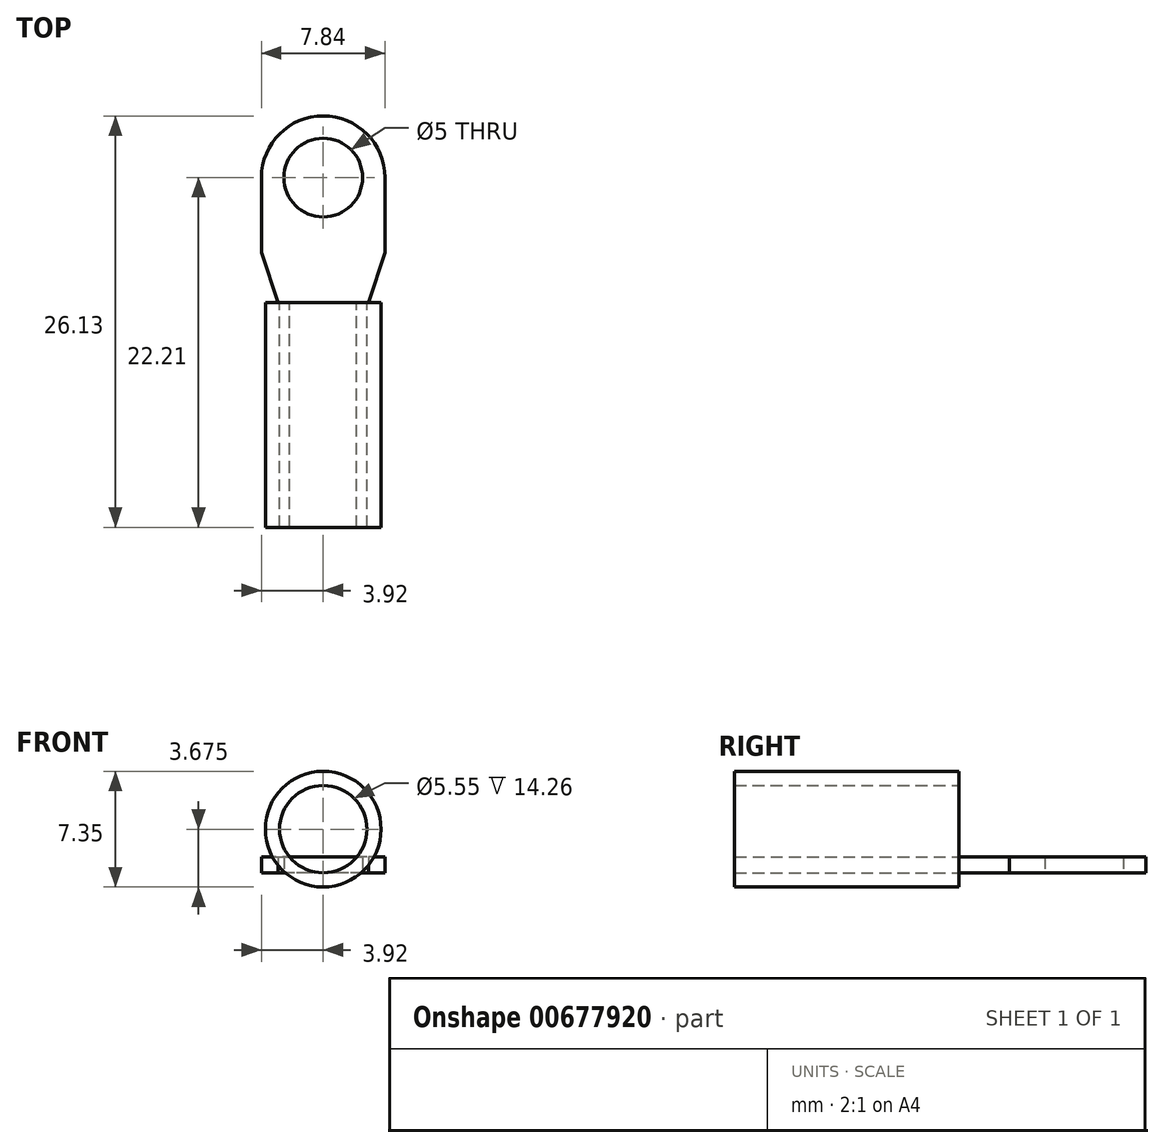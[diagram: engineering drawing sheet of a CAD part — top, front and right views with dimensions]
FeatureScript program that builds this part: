
annotation { "Feature Type Name" : "Feature", "Feature Type Description" : "" }
export const myFeature = defineFeature(function(context is Context, id is Id, definition is map)
    precondition{}
    {
        {
            var Q0;
            Q0=qCreatedBy(makeId("Top.planeOp"),FACE);
            var sketch = newSketch(context, id + "F0", { "sketchPlane" : qUnion([Q0])});
            skCircle(sketch, "E0", {"center": v(0, 0) * mm, "radius": 2.5 * mm});
            skCircle(sketch, "E1", {"center": v(0, 0) * mm, "radius": 3.92 * mm});
            skLineSegment(sketch, "E2", {"start": v(-3.92, 0) * mm, "end": v(-3.92, -4.75) * mm});
            skLineSegment(sketch, "E3", {"start": v(3.92, 0) * mm, "end": v(3.92, -4.75) * mm});
            skLineSegment(sketch, "E4", {"start": v(3.92, -4.75) * mm, "end": v(2.87, -7.95) * mm});
            skLineSegment(sketch, "E5", {"start": v(-3.92, -4.75) * mm, "end": v(-2.87, -7.95) * mm});
            skLineSegment(sketch, "E6", {"start": v(-2.87, -7.95) * mm, "end": v(2.87, -7.95) * mm});
            skSolve(sketch);
        }
        {
            var Q0;
            Q0 = qSketchRegion(id + "F0", true);
            extrude(context, id + "F1", {"entities" : qUnion([Q0]), "depth" : 1 * mm, "offsetDistance" : 25 * mm});
        }
        {
            var Q0;
            Q0=makeQuery(id+"F1.opExtrude","SWEPT_FACE",FACE,{"disambiguationData":[OSD([sQuery(id+"F0.wireOp",EDGE,"E6")])]});
            var sketch = newSketch(context, id + "F2", { "sketchPlane" : qUnion([Q0])});
            skCircle(sketch, "E7", {"center": v(0, 2.77) * mm, "radius": 3.67 * mm});
            skCircle(sketch, "E8", {"center": v(0, 2.77) * mm, "radius": 2.77 * mm});
            skSolve(sketch);
        }
        {
            var Q0;
            Q0 = qSketchRegion(id + "F2", true);
            extrude(context, id + "F3", {"entities" : qUnion([Q0]), "depth" : 14.26 * mm, "offsetDistance" : 25 * mm});
        }
        {
            var Q0;
            {var subQ0=sQuery(id+"F2.wireOp",EDGE,"E8");var subQ1=sQuery(id+"F0.wireOp",EDGE,"E6");var subQ2=makeQuery(id+"F2.imprint","INTERSECT",VERTEX,{"derivedFrom":[makeQuery(id+"F1.opExtrude","CAP_EDGE",EDGE,{"disambiguationData":[OSD([subQ1])],"isStart":true}),subQ0]});Q0=makeQuery(id+"F2.imprint","IMPRINT",FACE,{"disambiguationData":[TD([[makeQuery(id+"F2.imprint","IMPRINT",EDGE,{"disambiguationData":[TD([[subQ2,1.0]])],"derivedFrom":subQ0}),1.0]])]});}
            extrude(context, id + "F4", {"entities" : qUnion([Q0]), "depth" : 14.25 * mm, "offsetDistance" : 25 * mm});
        }
    });
